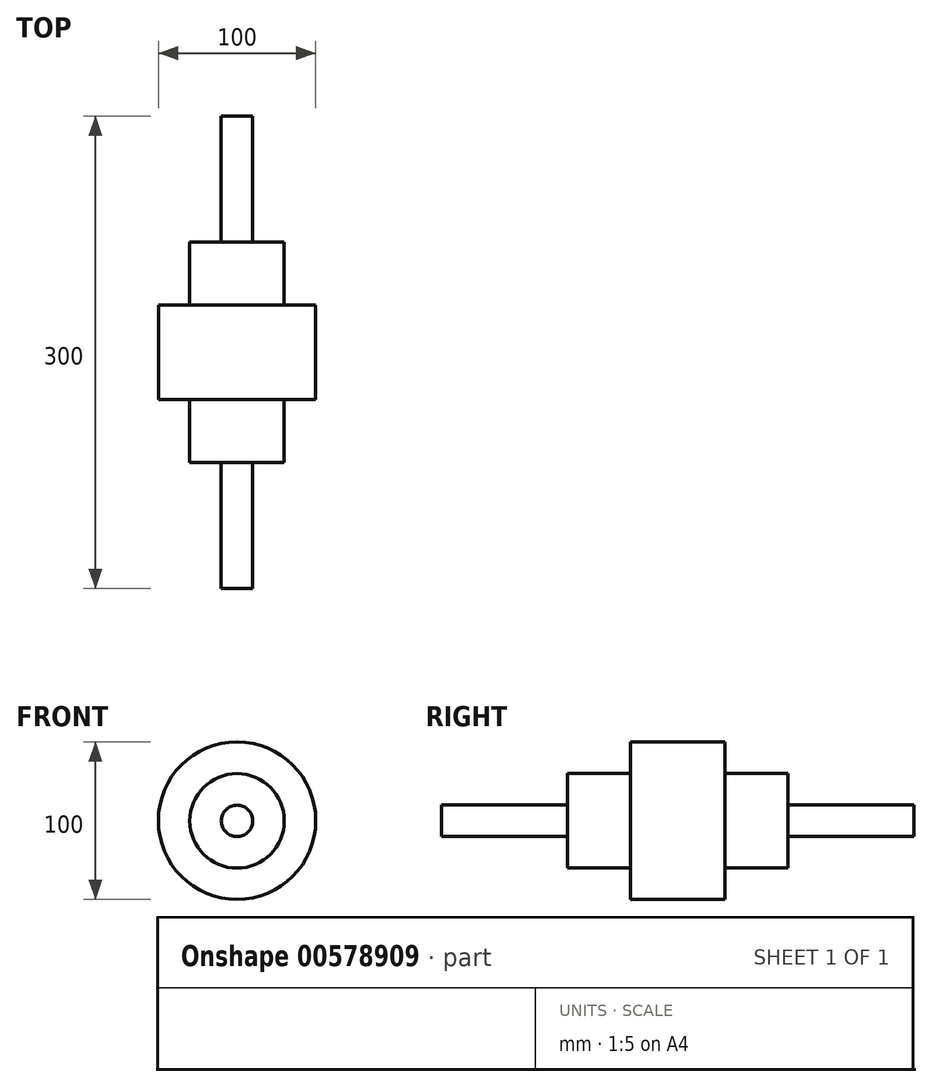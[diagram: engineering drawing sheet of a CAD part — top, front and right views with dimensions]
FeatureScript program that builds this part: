
annotation { "Feature Type Name" : "Feature", "Feature Type Description" : "" }
export const myFeature = defineFeature(function(context is Context, id is Id, definition is map)
    precondition{}
    {
        {
            var Q0;
            Q0=qCreatedBy(makeId("Front.planeOp"),FACE);
            var sketch = newSketch(context, id + "F0", { "sketchPlane" : qUnion([Q0])});
            skCircle(sketch, "E0", {"center": v(0, 0.14) * mm, "radius": 50 * mm});
            skSolve(sketch);
        }
        {
            var Q0;
            Q0 = qSketchRegion(id + "F0", true);
            extrude(context, id + "F1", {"entities" : qUnion([Q0]), "endBound" : BoundingType.SYMMETRIC, "oppositeDirection" : true, "depth" : (300 - (80 + 40) * 2) * mm, "offsetDistance" : 25 * mm});
        }
        {
            var Q0;
            Q0=makeQuery(id+"F1.opExtrude","CAP_FACE",FACE,{"disambiguationData":[OSD([sQuery(id+"F0.wireOp",EDGE,"E0")])],"isStart":false});
            var sketch = newSketch(context, id + "F2", { "sketchPlane" : qUnion([Q0])});
            skCircle(sketch, "E1", {"center": v(0, 0) * mm, "radius": 30 * mm});
            skSolve(sketch);
        }
        {
            var Q0;
            Q0=makeQuery(id+"F2.imprint","IMPRINT",FACE,{"disambiguationData":[TD([[makeQuery(id+"F2.imprint","IMPRINT",EDGE,{"derivedFrom":sQuery(id+"F2.wireOp",EDGE,"E1")}),1.0]])]});
            extrude(context, id + "F3", {"entities" : qUnion([Q0]), "operationType" : NewBodyOperationType.ADD, "depth" : 40 * mm, "offsetDistance" : 25 * mm});
        }
        {
            var Q0;
            Q0=makeQuery(id+"F3.opExtrude","CAP_FACE",FACE,{"disambiguationData":[OSD([sQuery(id+"F2.wireOp",EDGE,"E1")])],"isStart":false});
            var sketch = newSketch(context, id + "F4", { "sketchPlane" : qUnion([Q0])});
            skCircle(sketch, "E2", {"center": v(0, 0) * mm, "radius": 10 * mm});
            skSolve(sketch);
        }
        {
            var Q0;
            Q0 = qSketchRegion(id + "F4", true);
            extrude(context, id + "F5", {"entities" : qUnion([Q0]), "operationType" : NewBodyOperationType.ADD, "depth" : 80 * mm, "offsetDistance" : 25 * mm});
        }
        {
            var Q0;
            Q0=makeQuery(id+"F1.opExtrude","SWEPT_BODY",BODY,{"disambiguationData":[OSD([sQuery(id+"F0.wireOp",EDGE,"E0")])]});
            var Q1;
            Q1=qCreatedBy(makeId("Front.planeOp"),FACE);
            mirror(context, id + "F6", {"operationType" : NewBodyOperationType.ADD, "entities" : qUnion([Q0]), "mirrorPlane" : qUnion([Q1])});
        }
    });
